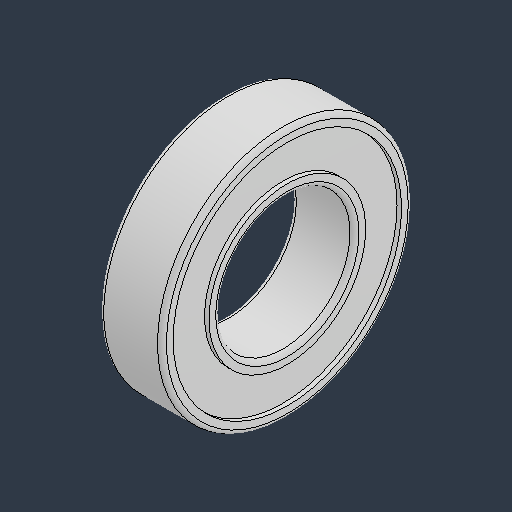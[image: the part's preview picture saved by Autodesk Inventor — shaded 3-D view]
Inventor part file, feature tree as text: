
AUTODESK INVENTOR PART (.ipt)
format: ipt  version: 2024.3 (Build 283343000, 343)  size: 152,576 bytes
history: native  units: in
note: dims shown in document units (in); Inventor stores cm internally (conversion verified against a paired STEP export)
features: fillet x1
ambient origin geometry x8: Origin, YZ Plane, XZ Plane, XY Plane, X Axis, Y Axis, Z Axis, Center Point
bodies: Solid1 (feature_tree)
feature tree (1):
  fillet  "Fillet1"  [1 undecoded]
note: 1 required parameter value undecoded (feature->parameter linkage not recoverable at this tier; creation-order binding heuristic only, values carry confidence <= 0.55)
